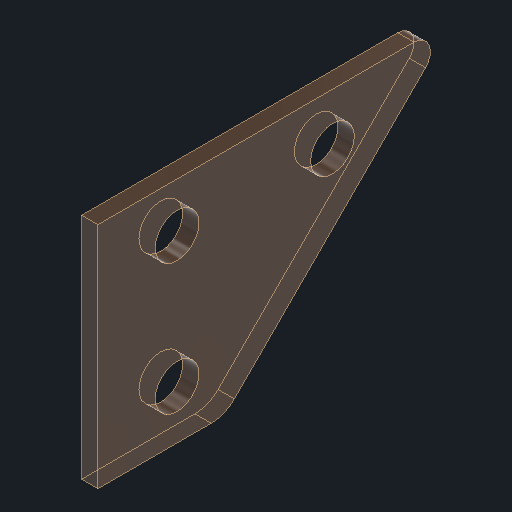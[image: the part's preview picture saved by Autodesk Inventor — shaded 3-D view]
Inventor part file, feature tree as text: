
AUTODESK INVENTOR PART (.ipt)
format: ipt  version: 2024 (Build 280153000, 153)  size: 115,712 bytes
history: native  units: in
note: dims shown in document units (in); Inventor stores cm internally (conversion verified against a paired STEP export)
features: other x3, sketch x3
ambient origin geometry x8: Origin, YZ Plane, XZ Plane, XY Plane, X Axis, Y Axis, Z Axis, Center Point
bodies: Solid1 (feature_tree)
feature tree (6):
  other  "sled-old.ipt"
  other  "Solid1::sled-old.ipt"
  other  "TaggingFeature1"
  sketch  "Sketch1"  dims[d0=0.3937in]
  sketch  "Sketch2"
  sketch  "Sketch3"
